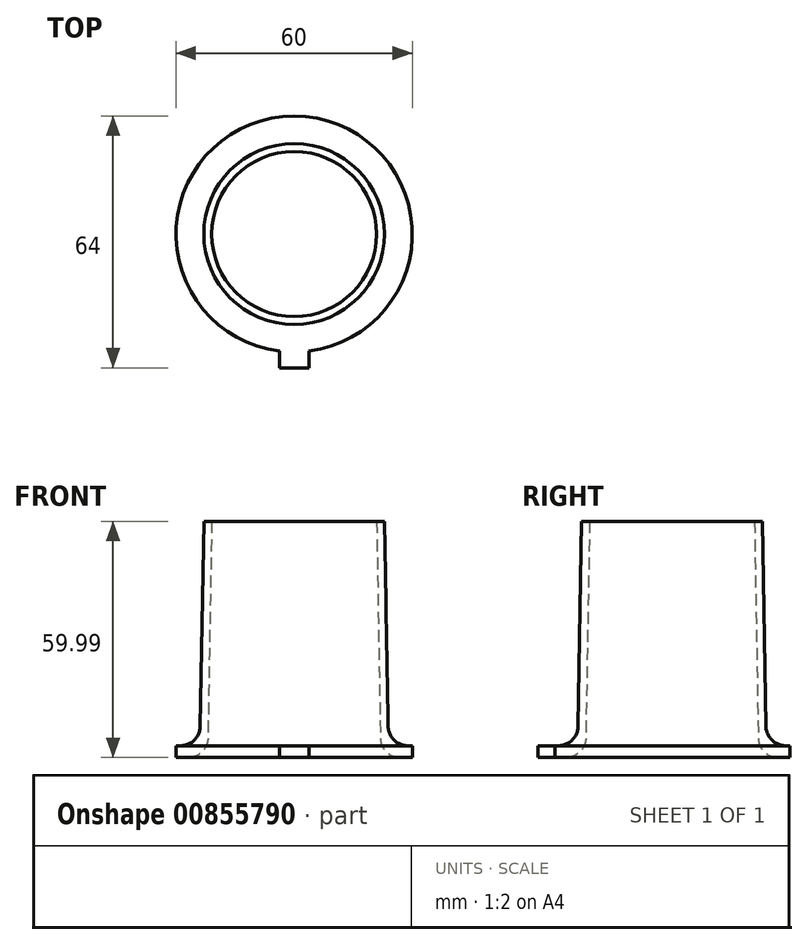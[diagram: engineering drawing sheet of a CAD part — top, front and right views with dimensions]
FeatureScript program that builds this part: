
annotation { "Feature Type Name" : "Feature", "Feature Type Description" : "" }
export const myFeature = defineFeature(function(context is Context, id is Id, definition is map)
    precondition{}
    {
        {
            var Q0;
            Q0=qCreatedBy(makeId("Front.planeOp"),FACE);
            var sketch = newSketch(context, id + "F0", { "sketchPlane" : qUnion([Q0])});
            skLineSegment(sketch, "E0", {"start": v(0, 0) * mm, "end": v(24, 0) * mm});
            skLineSegment(sketch, "E1", {"start": v(24, 0) * mm, "end": v(22.95, 60) * mm});
            skLineSegment(sketch, "E2", {"start": v(22.95, 60) * mm, "end": v(0, 60) * mm});
            skLineSegment(sketch, "E3", {"start": v(0, 60) * mm, "end": v(0, 0) * mm});
            skLineSegment(sketch, "E4", {"start": v(0, 121.43) * mm, "end": v(0, -13.9) * mm, "construction": true});
            skLineSegment(sketch, "E5", {"start": v(0, 0) * mm, "end": v(22, 0) * mm});
            skLineSegment(sketch, "E6", {"start": v(22, 0) * mm, "end": v(20.95, 60) * mm});
            skLineSegment(sketch, "E7", {"start": v(20.95, 60) * mm, "end": v(0, 60) * mm});
            skLineSegment(sketch, "E8.bottom", {"start": v(0, 0) * mm, "end": v(30, 0) * mm});
            skLineSegment(sketch, "E8.top", {"start": v(0, 3) * mm, "end": v(30, 3) * mm});
            skLineSegment(sketch, "E8.left", {"start": v(0, 0) * mm, "end": v(0, 3) * mm});
            skLineSegment(sketch, "E8.right", {"start": v(30, 0) * mm, "end": v(30, 3) * mm});
            skSolve(sketch);
        }
        {
            var Q0;
            {var subQ0=sQuery(id+"F0.wireOp",EDGE,"E8.bottom");Q0=makeQuery(id+"F0.imprint","IMPRINT",FACE,{"disambiguationData":[TD([[makeQuery(id+"F0.imprint","IMPRINT",EDGE,{"derivedFrom":subQ0}),1.0]])]});}
            var Q1;
            {var subQ0=sQuery(id+"F0.wireOp",EDGE,"E8.top");var subQ1=sQuery(id+"F0.wireOp",EDGE,"E1");var subQ2=makeQuery(id+"F0.imprint","INTERSECT",VERTEX,{"derivedFrom":[subQ1,subQ0]});Q1=makeQuery(id+"F0.imprint","IMPRINT",FACE,{"disambiguationData":[TD([[makeQuery(id+"F0.imprint","IMPRINT",EDGE,{"disambiguationData":[TD([[subQ2,-1.0]])],"derivedFrom":subQ1}),1.0]])]});}
            var Q2;
            {var subQ3=sQuery(id+"F0.wireOp",EDGE,"E6");var subQ5=sQuery(id+"F0.wireOp",EDGE,"E8.top");var subQ7=makeQuery(id+"F0.imprint","INTERSECT",VERTEX,{"derivedFrom":[subQ3,subQ5]});Q2=makeQuery(id+"F0.imprint","IMPRINT",FACE,{"disambiguationData":[TD([[makeQuery(id+"F0.imprint","IMPRINT",EDGE,{"disambiguationData":[TD([[subQ7,1.0]])],"derivedFrom":subQ3}),-1.0]])]});}
            var Q3;
            Q3=sQuery(id+"F0.wireOp",EDGE,"E4");
            revolve(context, id + "F1", {"surfaceOperationType" : NewSurfaceOperationType.NEW, "entities" : qUnion([Q0, Q1, Q2]), "axis" : qUnion([Q3]), "revolveType" : RevolveType.FULL});
        }
        {
            var Q0;
            Q0=makeQuery(id+"F1.opRevolve","SWEPT_FACE",FACE,{"disambiguationData":[OSD([sQuery(id+"F0.wireOp",EDGE,"E0"),sQuery(id+"F0.wireOp",EDGE,"E8.bottom")])]});
            var sketch = newSketch(context, id + "F2", { "sketchPlane" : qUnion([Q0])});
            skLineSegment(sketch, "E9.bottom", {"start": v(3.75, 26) * mm, "end": v(-3.75, 26) * mm});
            skLineSegment(sketch, "E9.top", {"start": v(3.75, 34) * mm, "end": v(-3.75, 34) * mm});
            skLineSegment(sketch, "E9.left", {"start": v(3.75, 26) * mm, "end": v(3.75, 34) * mm});
            skLineSegment(sketch, "E9.right", {"start": v(-3.75, 26) * mm, "end": v(-3.75, 34) * mm});
            skPoint(sketch, "E9.middle", {"position": v(0, 30) * mm});
            skSolve(sketch);
        }
        {
            var Q0;
            Q0 = qSketchRegion(id + "F2", true);
            extrude(context, id + "F3", {"entities" : qUnion([Q0]), "operationType" : NewBodyOperationType.ADD, "oppositeDirection" : true, "depth" : 3 * mm, "offsetDistance" : 25 * mm});
        }
        {
            var Q0;
            Q0=makeQuery(id+"F1.opRevolve","SWEPT_EDGE",EDGE,{"disambiguationData":[OSD([sQuery(id+"F0.wireOp",EDGE,"E1"),sQuery(id+"F0.wireOp",EDGE,"E8.top")])]});
            var Q1;
            Q1=makeQuery(id+"F1.opRevolve","SWEPT_EDGE",EDGE,{"disambiguationData":[OSD([sQuery(id+"F0.wireOp",EDGE,"E0"),sQuery(id+"F0.wireOp",EDGE,"E6")])]});
            fillet(context, id + "F4", {"entities" : qUnion([Q0, Q1]), "radius" : 5 * mm, "tangentPropagation" : true, "allowEdgeOverflow" : false});
        }
    });
